# Revit family: FU_Modular_Sandler_Flow 06050
name_source: partatom
category: Furniture
units: mm (PartAtom-declared; Revit-internal decimal feet)

## family parameters
Always vertical = Yes
Cut with Voids When Loaded = No
OmniClass Number = 23.40.20.00
OmniClass Title = General Furniture and Specialties
Render Appearance Source = Family Geometry
Room Calculation Point = No
Shared = No
Work Plane-Based = No

## types (1)
- Flow 06050
    Default Elevation = 0 mm  [stored 0 ft]
    Depth = 1150 mm  [stored 3.77297 ft]
    Description = Left-hand seat in the Flow modular seating series. Irregular shape with no backrest. Comfortable webbed seat.
    Height = 450 mm  [stored 1.47638 ft]
    Manufacturer = Sandler
    Model = Flow 06050
    URL = https://www.sandlerseating.com
    Width = 2130 mm  [stored 6.98819 ft]

note: [stored X ft] marks values corroborated as IEEE doubles in the binary element streams (Revit-internal decimal feet)

## geometry (parser evidence)
native form markers: Sweep x3
no freeform markers — native parametric forms only
